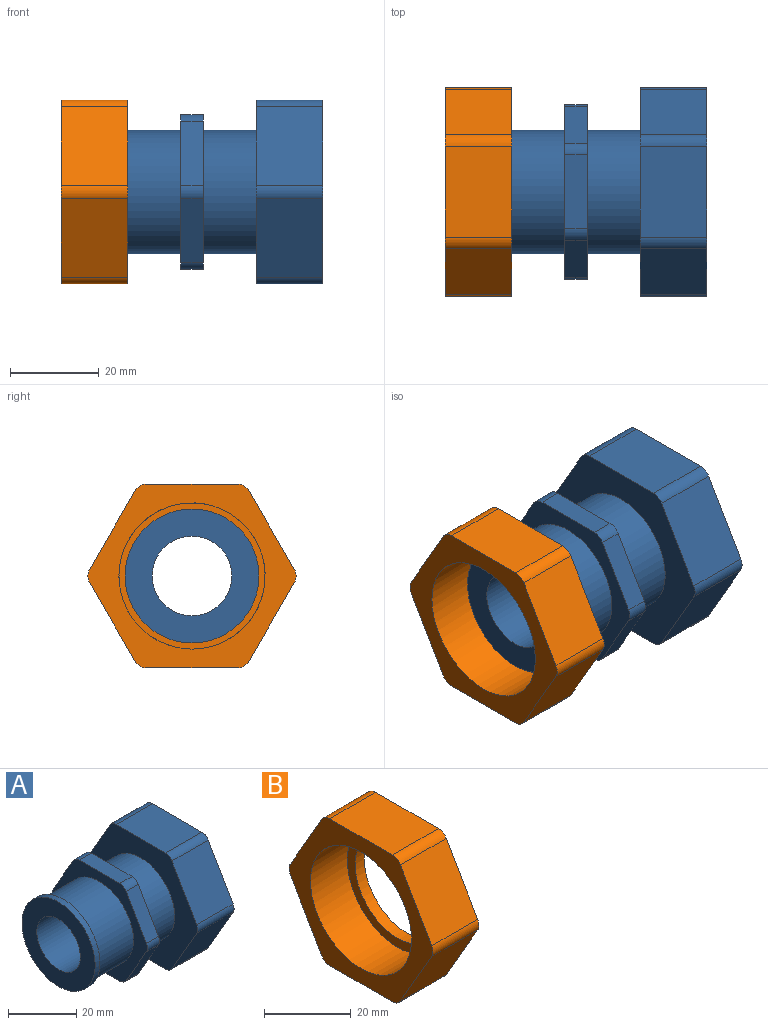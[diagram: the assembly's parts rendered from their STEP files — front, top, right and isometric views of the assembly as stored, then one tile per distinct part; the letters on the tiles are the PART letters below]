
ASSEMBLY  parts=2 mates=1
PART A: 36 faces, bbox 49x47x41.5 mm
  f0: plane 25.35x25.35mm, normal (1,0,0), area 250.3mm2, adj f1,f35
  f1: cylinder r=9mm len=37mm, axis (-1,0,0), area 2092.3mm2, adj f0,f34
  f2: cylinder r=13.95mm len=27.91mm, axis (-1,0,0), area 1315.2mm2, adj f15,f33
  f3: plane 16.71x5mm, normal (0,0,-1), area 83.5mm2, adj f4,f14,f15,f31
  f4: cylinder r=3mm len=5mm, axis (-1,0,0), area 15.7mm2, adj f3,f5,f15,f31
  f5: plane 14.47x8.36mm, normal (0,0.87,-0.5), area 83.5mm2, adj f4,f6,f15,f31
  f6: cylinder r=3mm len=5mm, axis (-1,0,0), area 15.7mm2, adj f5,f7,f15,f31
  f7: plane 14.47x8.36mm, normal (0,0.87,0.5), area 83.5mm2, adj f6,f8,f15,f31
  f8: cylinder r=3mm len=5mm, axis (-1,0,0), area 15.7mm2, adj f7,f9,f15,f31
  f9: plane 16.71x5mm, normal (0,0,1), area 83.5mm2, adj f8,f10,f15,f31
  f10: cylinder r=3mm len=5mm, axis (-1,0,0), area 15.7mm2, adj f9,f11,f15,f31
  f11: plane 14.47x8.36mm, normal (0,-0.87,0.5), area 83.5mm2, adj f10,f12,f15,f31
  f12: cylinder r=3mm len=5mm, axis (-1,0,0), area 15.7mm2, adj f11,f13,f15,f31
  f13: plane 14.47x8.36mm, normal (0,-0.87,-0.5), area 83.5mm2, adj f12,f14,f15,f31
  f14: cylinder r=3mm len=5mm, axis (-1,0,0), area 15.7mm2, adj f3,f13,f15,f31
  f15: plane 39.42x34.94mm, normal (-1,0,0), area 442.7mm2, adj f2,f3,f4,f5,f6,f7,f8,f9
  f16: plane 20.5x15mm, normal (0,0,-1), area 307.5mm2, adj f17,f27,f28,f29
  f17: cylinder r=3mm len=15mm, axis (-1,0,0), area 47.1mm2, adj f16,f18,f28,f29
  f18: plane 17.75x15mm, normal (0,0.87,-0.5), area 307.5mm2, adj f17,f19,f28,f29
  f19: cylinder r=3mm len=15mm, axis (-1,0,0), area 47.1mm2, adj f18,f20,f28,f29
  f20: plane 17.75x15mm, normal (0,0.87,0.5), area 307.5mm2, adj f19,f21,f28,f29
  f21: cylinder r=3mm len=15mm, axis (-1,0,0), area 47.1mm2, adj f20,f22,f28,f29
  f22: plane 20.5x15mm, normal (0,0,1), area 307.5mm2, adj f21,f23,f28,f29
  f23: cylinder r=3mm len=15mm, axis (-1,0,0), area 47.1mm2, adj f22,f24,f28,f29
  f24: plane 17.75x15mm, normal (0,-0.87,0.5), area 307.5mm2, adj f23,f25,f28,f29
  f25: cylinder r=3mm len=15mm, axis (-1,0,0), area 47.1mm2, adj f24,f26,f28,f29
  f26: plane 17.75x15mm, normal (0,-0.87,-0.5), area 307.5mm2, adj f25,f27,f28,f29
  f27: cylinder r=3mm len=15mm, axis (-1,0,0), area 47.1mm2, adj f16,f26,f28,f29
  f28: plane 47x41.5mm, normal (1,0,0), area 984.1mm2, adj f16,f17,f18,f19,f20,f21,f22,f23
  f29: plane 47x41.5mm, normal (-1,0,0), area 877.1mm2, adj f16,f17,f18,f19,f20,f21,f22,f23
  f30: cylinder r=13.95mm len=27.91mm, axis (1,0,0), area 1052.2mm2, adj f29,f31
  f31: plane 39.42x34.94mm, normal (1,0,0), area 442.7mm2, adj f3,f4,f5,f6,f7,f8,f9,f10
  f32: cylinder r=15.12mm len=30.24mm, axis (-1,0,0), area 190mm2, adj f33,f34
  f33: plane 30.24x30.24mm, normal (1,0,0), area 106.4mm2, adj f2,f32
  f34: plane 30.24x30.24mm, normal (-1,0,0), area 463.7mm2, adj f1,f32
  f35: cylinder r=12.68mm len=25.35mm, axis (1,0,0), area 955.7mm2, adj f0,f28
PART B: 17 faces, bbox 15x47x41.5 mm
  f0: cylinder r=16.5mm len=33mm, axis (1,0,0), area 1244.1mm2, adj f13,f15
  f1: plane 20.5x15mm, normal (0,0,-1), area 307.5mm2, adj f2,f12,f13,f14
  f2: cylinder r=3mm len=15mm, axis (1,0,0), area 47.1mm2, adj f1,f3,f13,f14
  f3: plane 17.75x15mm, normal (0,0.87,-0.5), area 307.5mm2, adj f2,f4,f13,f14
  f4: cylinder r=3mm len=15mm, axis (1,0,0), area 47.1mm2, adj f3,f5,f13,f14
  f5: plane 17.75x15mm, normal (0,0.87,0.5), area 307.5mm2, adj f4,f6,f13,f14
  f6: cylinder r=3mm len=15mm, axis (1,0,0), area 47.1mm2, adj f5,f7,f13,f14
  f7: plane 20.5x15mm, normal (0,0,1), area 307.5mm2, adj f6,f8,f13,f14
  f8: cylinder r=3mm len=15mm, axis (1,0,0), area 47.1mm2, adj f7,f9,f13,f14
  f9: plane 17.75x15mm, normal (0,-0.87,0.5), area 307.5mm2, adj f8,f10,f13,f14
  f10: cylinder r=3mm len=15mm, axis (1,0,0), area 47.1mm2, adj f9,f11,f13,f14
  f11: plane 17.75x15mm, normal (0,-0.87,-0.5), area 307.5mm2, adj f10,f12,f13,f14
  f12: cylinder r=3mm len=15mm, axis (1,0,0), area 47.1mm2, adj f1,f11,f13,f14
  f13: plane 47x41.5mm, normal (-1,0,0), area 633.6mm2, adj f0,f1,f2,f3,f4,f5,f6,f7
  f14: plane 47x41.5mm, normal (1,0,0), area 877.1mm2, adj f1,f2,f3,f4,f5,f6,f7,f8
  f15: plane 33x33mm, normal (-1,0,0), area 243.5mm2, adj f0,f16
  f16: cylinder r=13.95mm len=27.91mm, axis (1,0,0), area 263mm2, adj f14,f15
PLACE A t=(-85.89,-44.81,-44.79)mm
PLACE B t=(-85.89,-44.81,-44.79)mm
MATE revolute B.f0 <-> A.f1  axis (-1,0,0) through (-49.39,-44.81,-44.79)mm
